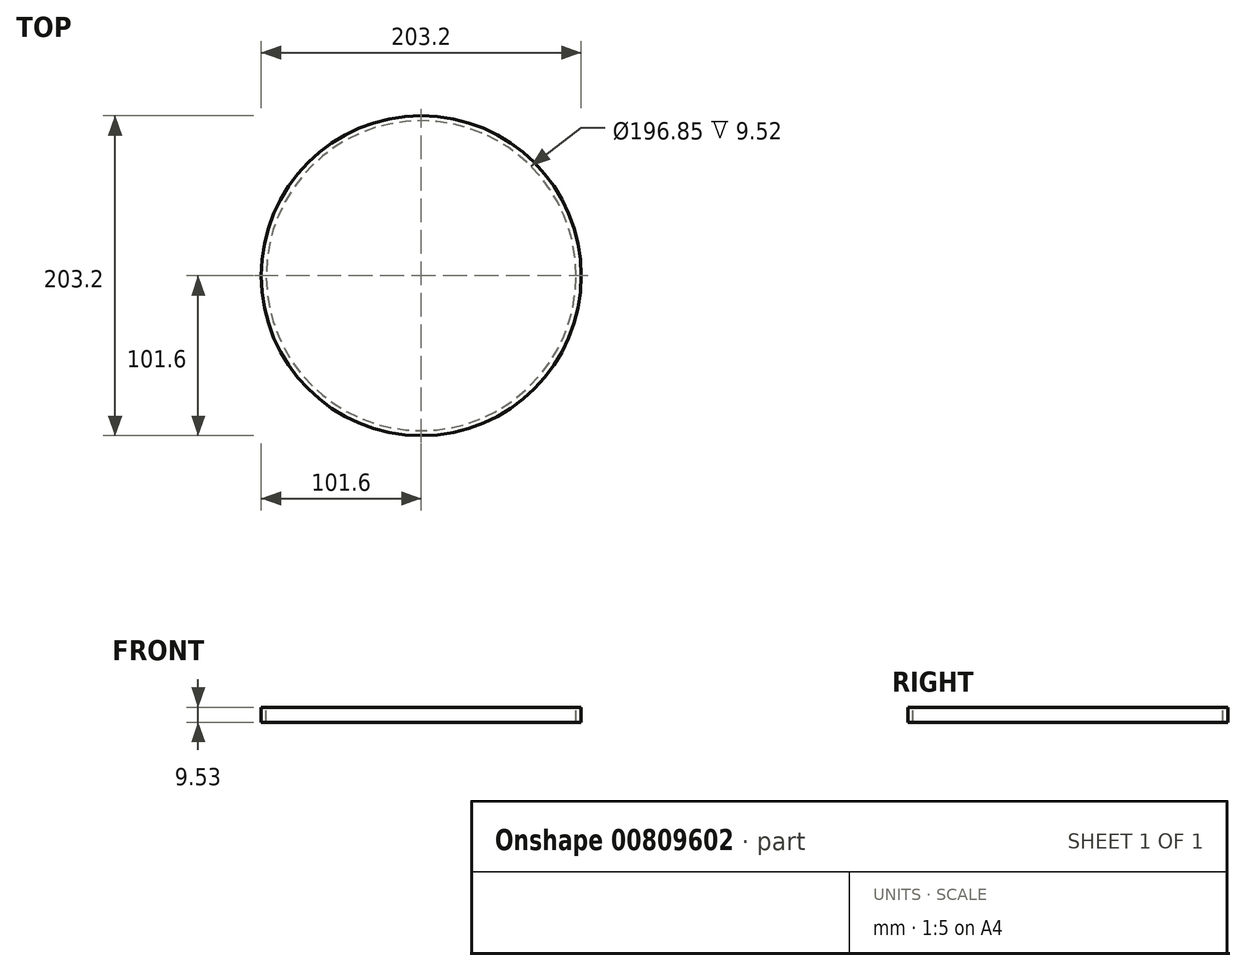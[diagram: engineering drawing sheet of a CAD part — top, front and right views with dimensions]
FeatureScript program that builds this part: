
annotation { "Feature Type Name" : "Feature", "Feature Type Description" : "" }
export const myFeature = defineFeature(function(context is Context, id is Id, definition is map)
    precondition{}
    {
        {
            var Q0;
            Q0=qCreatedBy(makeId("Top.planeOp"),FACE);
            var sketch = newSketch(context, id + "F0", { "sketchPlane" : qUnion([Q0])});
            skCircle(sketch, "E0", {"center": v(0, 0) * mm, "radius": 101.6 * mm});
            skCircle(sketch, "E1", {"center": v(0, 0) * mm, "radius": 98.43 * mm});
            skSolve(sketch);
        }
        {
            var Q0;
            Q0=makeQuery(id+"F0.imprint","IMPRINT",FACE,{"disambiguationData":[TD([[makeQuery(id+"F0.imprint","IMPRINT",EDGE,{"derivedFrom":sQuery(id+"F0.wireOp",EDGE,"E0")}),1.0]])]});
            extrude(context, id + "F1", {"entities" : qUnion([Q0]), "oppositeDirection" : true, "depth" : 9.52 * mm, "offsetDistance" : 25.4 * mm});
        }
        {
            var Q0;
            Q0=qCreatedBy(makeId("Top.planeOp"),FACE);
            var sketch = newSketch(context, id + "F2", { "sketchPlane" : qUnion([Q0])});
            skCircle(sketch, "E2", {"center": v(0, 0) * mm, "radius": 98.43 * mm});
            skSolve(sketch);
        }
        {
            var Q0;
            Q0 = qSketchRegion(id + "F2", true);
            var Q1;
            Q1=makeQuery(id+"F2.imprint","IMPRINT",FACE,{"disambiguationData":[TD([[makeQuery(id+"F2.imprint","IMPRINT",EDGE,{"derivedFrom":sQuery(id+"F2.wireOp",EDGE,"E2")}),1.0]])]});
            extrude(context, id + "F3", {"entities" : qUnion([Q0, Q1]), "operationType" : NewBodyOperationType.ADD, "oppositeDirection" : true, "depth" : 1 / 203.2 * mm, "offsetDistance" : 25.4 * mm});
        }
    });
